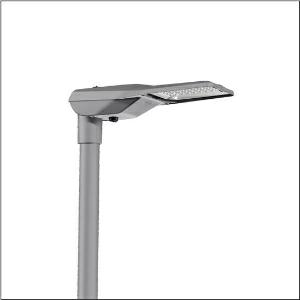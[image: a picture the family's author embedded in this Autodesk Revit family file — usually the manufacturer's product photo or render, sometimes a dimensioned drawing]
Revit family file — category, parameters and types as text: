
# Revit family: streetlight_sl_21_iq_mini___st1_0a_5xe2d61y08hb_d678
name_source: partatom
category: Lighting Fixtures
units: mm (PartAtom-declared; Revit-internal decimal feet)

## family parameters
Cut with Voids When Loaded = No
Host = Face
Light Source = No
Part Type = Normal
Room Calculation Point = No
Round Connector Dimension = Use Diameter
Shared = No

## types (1)
- --- (1 x LED, 8460 lm, 71 W, 2700K)
    Apparent Load = 71 VA
    CIE Flux Codes = 37 72 97 100 100
    Color Rendering = 70
    Color Temperature = 2700K
    Default Elevation = 1800 mm
    Description = Streetlight SL 21 iQ mini, mast luminaire, primary light control with lens, of PMMA, primary optical cover: cover, of toughened safety glass, transparent, light distribution: ST1.0a, light emission: direct distribution, primary light characteristic: asymmetric, installation type: post-top, side-entry, LED, High Power LED, rated luminous flux: 8.460lm, luminous efficacy: 119lm/W, light colour: 727, colour temperature: 2700K, control: pre-setting: logarithmic dimming characteristic, Street-Remote, Auto-Match, Temp-Guard, Lumen-Switch, Night-Set, Smart-Wire, Light-Fading, Desk-Remote (wireless, voltage-free reading and setting of iQ features in the workshop via application-optimized NFC function/RFID function), optimised constant luminous flux control (CLO 2.0), mains connection: 220..240V, AC, 50/60Hz, start of lifetime: 71W, end of service life: 75W, reduction: 30W, luminaire housing, of diecast aluminium, powder-coated, Siteco® metallic grey (DB 702S), corrosivity category C5 mid according to DIN EN ISO 12944, please order mast flange separately, inclination adjustable: 0°, 5°, 10°, 15°, sealing non-destructively replaceable, multi-level sealing system, length: 628mm, width: 235mm, height: 110mm, mast flange for spigot size: 42mm (side-entry): 5XC10008XM4, 60/48mm (side-entry/post-top): 5XC10108XM2, 76/60mm (side-entry/post-top): 5XC10108XM1, Smart Interface below and above, protection rating (complete): IP66, insulation class (complete): insulation class II (safety insulation), certification: CE, ENEC, ENEC+, VDE, impact resistance: IK09, permissible operating ambient temperature for outdoor applications: -40..+50°C, standard-compliant lighting for roads and squares, packaging unit: 1 piece

Light Distribution: ST1.0a
    Height = 110 mm
    Lamp = 1 x LED
    Lamp Light Flux = 8460 lm
    Lamp Power = 71 W
    Lamp count = 1
    Length = 625 mm
    Luminous efficacy = 119 lm/W
    Manufacturer = Siteco
    ModVariant = No
    Model = 5XE2D61Y08HB
    Number of Poles = 1
    OnlyDefault = Yes
    Power Factor = 1
    Product Name = Streetlight SL 21 iQ mini | ST1.0a
    Product group = mast luminaire | pylon top
    ProductGroupID = 6100
    Protection Class = Protection class II
    Protection Degree = IP 66
    RLX_Detail_Level = 1
    RLX_Emergency_Light_Flux = 0 lm
    RLX_Emergency_Type = 0
    RLX_Emergency_Type_DB = No
    RlxData = <blob elided: 92333 chars, md5=dd484ae0>
    Socket = socket
    Standby Power = 0 W
    System Light Flux = 8460 lm
    System Power = 71 W
    Type Comments = factory setting: luminous flux: 100 % | dim-lin: 254 | 716 mA
    Type Image = l_1003514.jpg
    URL = http://relux.com
    VarID = @adj_083801
    Voltage = 0 V
    Weight = 0.00 kg
    Width = 234 mm

## geometry (parser evidence)
native form markers: Blend x4, Sweep x11
no freeform markers — native parametric forms only
